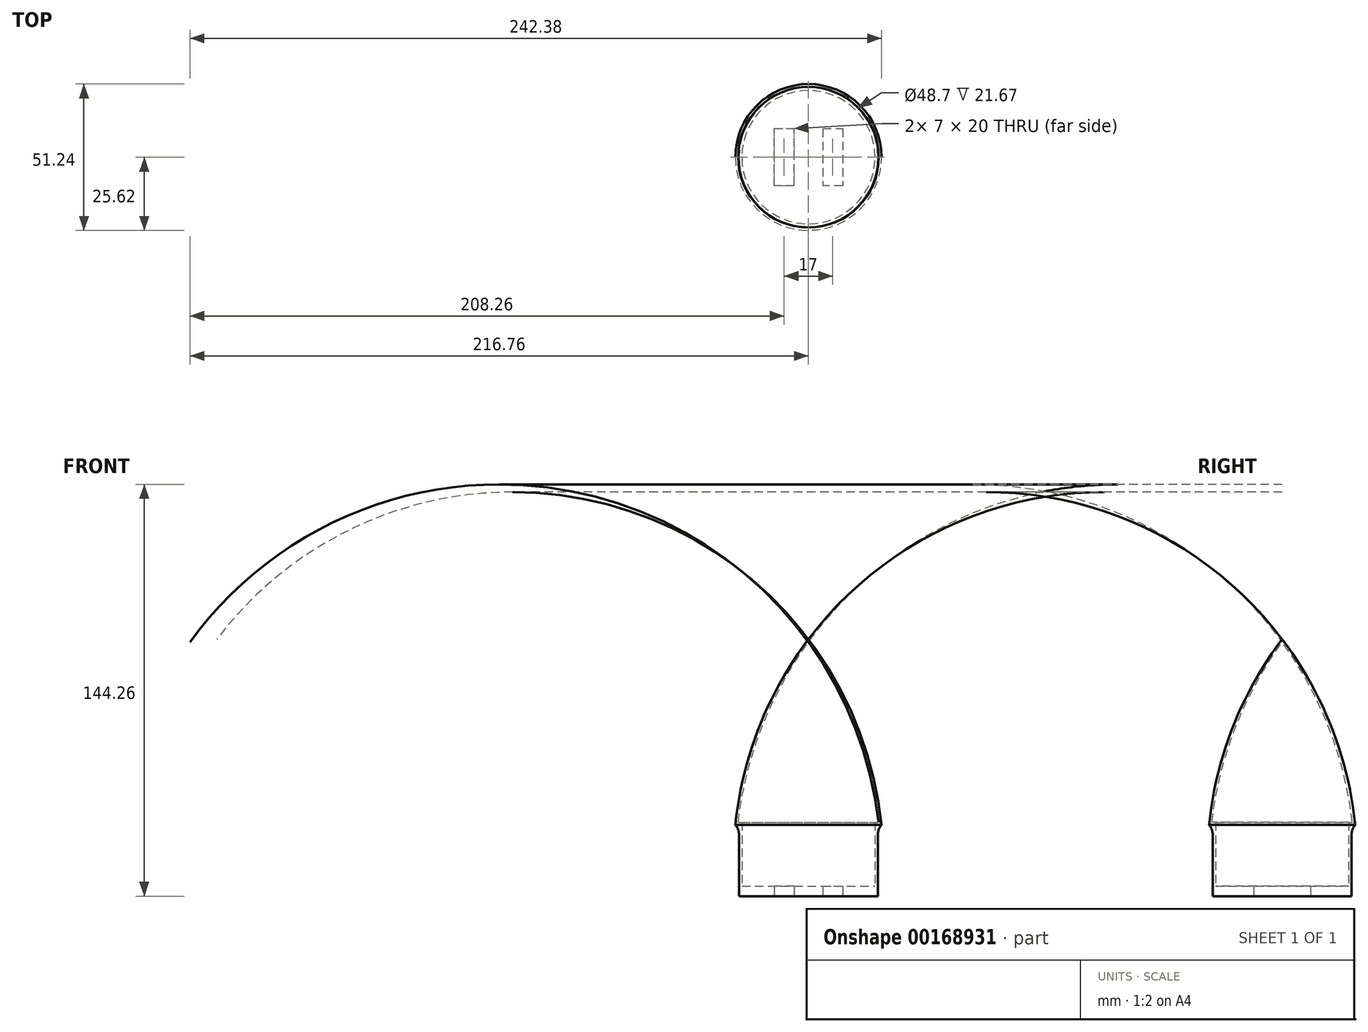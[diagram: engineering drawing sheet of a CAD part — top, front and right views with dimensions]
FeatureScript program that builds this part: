
annotation { "Feature Type Name" : "Feature", "Feature Type Description" : "" }
export const myFeature = defineFeature(function(context is Context, id is Id, definition is map)
    precondition{}
    {
        {
            var Q0;
            Q0=qCreatedBy(makeId("Front.planeOp"),FACE);
            var sketch = newSketch(context, id + "F0", { "sketchPlane" : qUnion([Q0])});
            skLineSegment(sketch, "E0", {"start": v(0, 0) * mm, "end": v(0, 90) * mm});
            skLineSegment(sketch, "E1", {"start": v(0, 0) * mm, "end": v(24.35, 0) * mm});
            skLineSegment(sketch, "E2", {"start": v(24.35, 0) * mm, "end": v(24.35, 25) * mm});
            skLineSegment(sketch, "E3", {"start": v(0, 3.5) * mm, "end": v(23.35, 3.5) * mm});
            skLineSegment(sketch, "E4", {"start": v(23.35, 3.5) * mm, "end": v(23.35, 25) * mm});
            skLineSegment(sketch, "E5", {"start": v(24.35, 25) * mm, "end": v(25.62, 25) * mm});
            skLineSegment(sketch, "E6", {"start": v(23.35, 25) * mm, "end": v(23.35, 25.9) * mm});
            skLineSegment(sketch, "E7", {"start": v(23.35, 25.9) * mm, "end": v(24.35, 25.9) * mm});
            skLineSegment(sketch, "E8", {"start": v(24.35, 25.9) * mm, "end": v(24.62, 25.9) * mm});
            skArc(sketch, "E9", {"start": v(25.62, 25) * mm, "mid": v(17.26, 59.25) * mm, "end": v(0, 90) * mm});
            skArc(sketch, "E10", {"start": v(24.62, 25.9) * mm, "mid": v(16.37, 59.03) * mm, "end": v(0, 89) * mm});
            skSolve(sketch);
        }
        {
            var Q0;
            {var subQ0=sQuery(id+"F0.wireOp",EDGE,"E1");Q0=makeQuery(id+"F0.imprint","IMPRINT",FACE,{"disambiguationData":[TD([[makeQuery(id+"F0.imprint","IMPRINT",EDGE,{"derivedFrom":subQ0}),1.0]])]});}
            var Q1;
            Q1=sQuery(id+"F0.wireOp",EDGE,"E0");
            revolve(context, id + "F1", {"entities" : qUnion([Q0]), "axis" : qUnion([Q1]), "revolveType" : RevolveType.FULL});
        }
        {
            var Q0;
            Q0=makeQuery(id+"F1.opRevolve","SWEPT_FACE",FACE,{"disambiguationData":[OSD([sQuery(id+"F0.wireOp",EDGE,"E1")])]});
            var sketch = newSketch(context, id + "F2", { "sketchPlane" : qUnion([Q0])});
            skLineSegment(sketch, "E11", {"start": v(0, 0) * mm, "end": v(5, 0) * mm, "construction": true});
            skLineSegment(sketch, "E12", {"start": v(0, 0) * mm, "end": v(-5, 0) * mm, "construction": true});
            skLineSegment(sketch, "E13", {"start": v(-5, 0) * mm, "end": v(-5, 10) * mm});
            skLineSegment(sketch, "E14", {"start": v(-5, 0) * mm, "end": v(-5, -10) * mm});
            skLineSegment(sketch, "E15", {"start": v(5, 0) * mm, "end": v(5, 10) * mm});
            skLineSegment(sketch, "E16", {"start": v(5, 0) * mm, "end": v(5, -10) * mm});
            skLineSegment(sketch, "E17", {"start": v(-5, 10) * mm, "end": v(-12, 10) * mm});
            skLineSegment(sketch, "E18", {"start": v(-12, 10) * mm, "end": v(-12, -10) * mm});
            skLineSegment(sketch, "E19", {"start": v(-12, -10) * mm, "end": v(-5, -10) * mm});
            skLineSegment(sketch, "E20", {"start": v(5, -10) * mm, "end": v(12, -10) * mm});
            skLineSegment(sketch, "E21", {"start": v(12, -10) * mm, "end": v(12, 10) * mm});
            skLineSegment(sketch, "E22", {"start": v(12, 10) * mm, "end": v(5, 10) * mm});
            skSolve(sketch);
        }
        {
            var Q0;
            Q0 = qSketchRegion(id + "F2", true);
            extrude(context, id + "F3", {"entities" : qUnion([Q0]), "operationType" : NewBodyOperationType.REMOVE, "oppositeDirection" : true, "depth" : 4 * mm});
        }
        {
            var Q0;
            Q0=makeQuery(id+"F1.opRevolve","SWEPT_EDGE",EDGE,{"disambiguationData":[OSD([sQuery(id+"F0.wireOp",EDGE,"E2"),sQuery(id+"F0.wireOp",EDGE,"E5")])]});
            fillet(context, id + "F4", {"entities" : qUnion([Q0]), "radius" : 5 * mm, "tangentPropagation" : true, "allowEdgeOverflow" : false});
        }
    });
